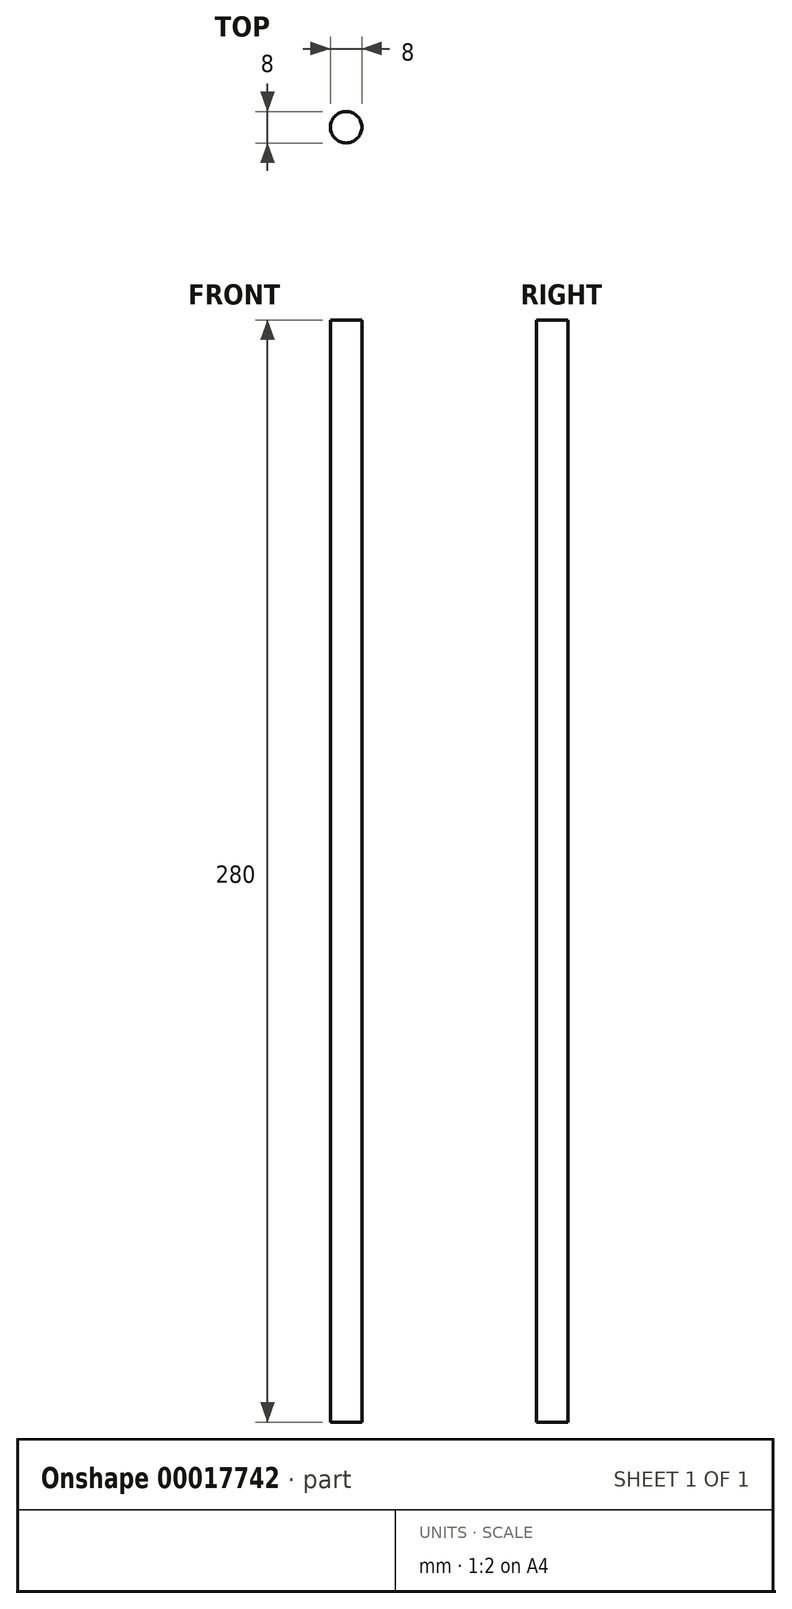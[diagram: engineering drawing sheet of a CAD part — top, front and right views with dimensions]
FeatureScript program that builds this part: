
annotation { "Feature Type Name" : "Feature", "Feature Type Description" : "" }
export const myFeature = defineFeature(function(context is Context, id is Id, definition is map)
    precondition{}
    {
        {
            var Q0;
            Q0=qCreatedBy(makeId("Top.planeOp"),FACE);
            var sketch = newSketch(context, id + "F0", { "sketchPlane" : qUnion([Q0])});
            skCircle(sketch, "E0", {"center": v(0, 0) * mm, "radius": 4 * mm});
            skSolve(sketch);
        }
        {
            var Q0;
            Q0=qSketchRegion(id+"F0",true);
            extrude(context, id + "F1", {"entities" : qUnion([Q0]), "depth" : 280 * mm});
        }
    });
